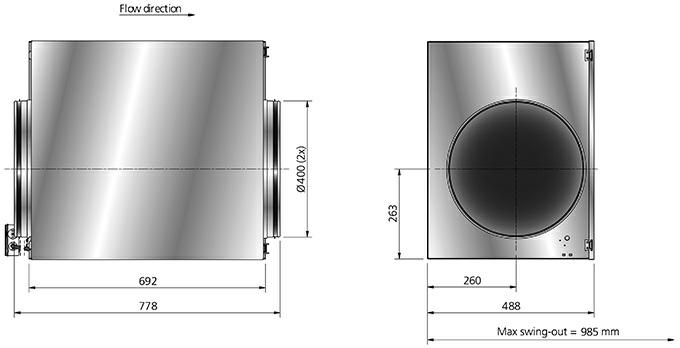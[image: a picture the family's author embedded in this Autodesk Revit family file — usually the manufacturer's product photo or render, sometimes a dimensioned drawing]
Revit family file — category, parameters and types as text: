
# Revit family: IRE 500 E3 ErP AC_7900044
name_source: partatom
category: Mechanical Equipment
revit_build: Autodesk Revit MEP 2014 (Build: 20130308_1515(x64)
units: mm (PartAtom-declared; Revit-internal decimal feet)

## types (1)
- IRE 500 E3 ErP AC
    Capacitor = - μF
    Current = 4 A
    Depth = 780 mm  [stored 2.55906 ft]
    Description = Insulated duct fans with circular connections
    Diameter = 500 mm  [stored 1.64042 ft]
    Frequency = 50 Hz
    Height = 584 mm  [stored 1.91601 ft]
    Main Material = Steel, Galvanized
    Max. temperature of transported air = 50 °C
    Max. temperature of transported air when speed controlled = 50 °C
    Phase = 3
    Power = 1800 W
    Sound pressure level at 3 m = 52 dB(A)
    Speed = 1380 rpm
    Voltage = 400 V
    Voltage range = 380-415 V
    Weight = 68.20 kg
    Width = 907 mm  [stored 2.97572 ft]
    Wiring diagram = Y 4040004 / Δ 4040003

note: [stored X ft] marks values corroborated as IEEE doubles in the binary element streams (Revit-internal decimal feet)

## geometry (parser evidence)
native form markers: Sweep x5
no freeform markers — native parametric forms only
